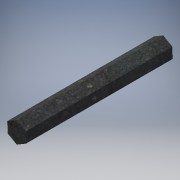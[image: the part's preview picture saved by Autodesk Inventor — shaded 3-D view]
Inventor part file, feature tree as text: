
AUTODESK INVENTOR PART (.ipt)
format: ipt  version: 2016 (Build 200138000, 138)  size: 102,400 bytes
history: native  units: in
note: dims shown in document units (in); Inventor stores cm internally (conversion verified against a paired STEP export)
features: extrude x1, sketch x1
ambient origin geometry x8: Origin, YZ Plane, XZ Plane, XY Plane, X Axis, Y Axis, Z Axis, Center Point
bodies: Solid1 (feature_tree)
feature tree (2):
  extrude  "Extrusion1"  Depth=4.0in TaperAngle=0.0deg
  sketch  "Sketch1"  dims[d0=0.5in d1=4.0in d2=0.0in]
